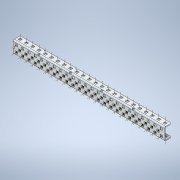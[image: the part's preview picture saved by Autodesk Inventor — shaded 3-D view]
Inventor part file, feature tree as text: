
AUTODESK INVENTOR PART (.ipt)
format: ipt  version: 2020 (Build 240168000, 168)  size: 1,409,024 bytes
history: native  units: in
note: dims shown in document units (in); Inventor stores cm internally (conversion verified against a paired STEP export)
features: other x123, plane x7, pattern_linear x4, split x1, sheet_metal_op x1
ambient origin geometry x8: Origin, YZ Plane, XZ Plane, XY Plane, X Axis, Y Axis, Z Axis, Center Point
bodies: Solid1 (feature_tree)
feature tree (136):
  other  "Work Axis1"
  pattern_linear  "Rectangular Pattern1"  Count1=24 Spacing1=0.5in
  other  "Work Axis72"
  pattern_linear  "Rectangular Pattern2"  Count1=24 Spacing1=0.5in
  pattern_linear  "Rectangular Pattern3"  Count1=24 Spacing1=0.5in
  other  "Work Axis141"
  pattern_linear  "Rectangular Pattern4"  Count1=23 Spacing1=0.5in
  plane  "Work Plane7"
  split  "Split1"
  plane  "Work Plane1"
  plane  "Work Plane2"
  other  "Work Point1"
  other  "Work Axis2"
  other  "Work Axis3"
  other  "Work Axis4"
  other  "Work Axis5"
  other  "Work Axis6"
  other  "Work Axis7"
  other  "Work Axis8"
  other  "Work Axis9"
  other  "Work Axis10"
  other  "Work Axis11"
  other  "Work Axis12"
  other  "Work Axis13"
  other  "Work Axis14"
  other  "Work Axis15"
  other  "Work Axis16"
  other  "Work Axis17"
  other  "Work Axis18"
  other  "Work Axis19"
  other  "Work Axis20"
  other  "Work Axis21"
  other  "Work Axis22"
  other  "Work Axis23"
  other  "Work Axis24"
  other  "Work Axis36"
  other  "Work Axis37"
  other  "Work Axis38"
  other  "Work Axis39"
  other  "Work Axis40"
  other  "Work Axis41"
  other  "Work Axis42"
  other  "Work Axis43"
  other  "Work Axis44"
  other  "Work Axis45"
  other  "Work Axis46"
  other  "Work Axis47"
  other  "Work Axis48"
  other  "Work Axis49"
  other  "Work Axis50"
  other  "Work Axis51"
  other  "Work Axis52"
  other  "Work Axis53"
  other  "Work Axis54"
  other  "Work Axis55"
  other  "Work Axis56"
  other  "Work Axis57"
  other  "Work Axis58"
  other  "Work Axis59"
  plane  "Work Plane3"
  plane  "Work Plane4"
  other  "Work Point2"
  other  "Work Axis71"
  other  "Work Point3"
  other  "Work Axis73"
  other  "Work Axis74"
  other  "Work Axis75"
  other  "Work Axis76"
  other  "Work Axis77"
  other  "Work Axis78"
  other  "Work Axis79"
  other  "Work Axis80"
  other  "Work Axis81"
  other  "Work Axis82"
  other  "Work Axis83"
  other  "Work Axis84"
  other  "Work Axis85"
  other  "Work Axis86"
  other  "Work Axis87"
  other  "Work Axis88"
  other  "Work Axis89"
  other  "Work Axis90"
  other  "Work Axis91"
  other  "Work Axis92"
  other  "Work Axis93"
  other  "Work Axis94"
  other  "Work Axis95"
  other  "Work Axis107"
  other  "Work Axis108"
  other  "Work Axis109"
  other  "Work Axis110"
  other  "Work Axis111"
  other  "Work Axis112"
  other  "Work Axis113"
  other  "Work Axis114"
  other  "Work Axis115"
  other  "Work Axis116"
  other  "Work Axis117"
  other  "Work Axis118"
  other  "Work Axis119"
  other  "Work Axis120"
  other  "Work Axis121"
  other  "Work Axis122"
  other  "Work Axis123"
  other  "Work Axis124"
  other  "Work Axis125"
  other  "Work Axis126"
  other  "Work Axis127"
  other  "Work Axis128"
  other  "Work Axis129"
  plane  "Work Plane5"
  plane  "Work Plane6"
  other  "Work Point4"
  other  "Work Axis142"
  other  "Work Axis143"
  other  "Work Axis144"
  other  "Work Axis145"
  other  "Work Axis146"
  other  "Work Axis147"
  other  "Work Axis148"
  other  "Work Axis149"
  other  "Work Axis150"
  other  "Work Axis151"
  other  "Work Axis152"
  other  "Work Axis153"
  other  "Work Axis154"
  other  "Work Axis155"
  other  "Work Axis156"
  other  "Work Axis157"
  other  "Work Axis158"
  other  "Work Axis159"
  other  "Work Axis160"
  other  "Work Axis161"
  other  "Work Axis162"
  other  "Work Axis163"
  sheet_metal_op  "Fold1"
